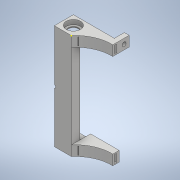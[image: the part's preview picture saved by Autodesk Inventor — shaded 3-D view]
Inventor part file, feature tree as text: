
AUTODESK INVENTOR PART (.ipt)
format: ipt  version: 2020 (Build 240168000, 168)  size: 626,176 bytes
history: native  units: mm
features: extrude x22, sketch x22, fillet x4
ambient origin geometry x8: Origin, YZ Plane, XZ Plane, XY Plane, X Axis, Y Axis, Z Axis, Center Point
bodies: Solid1 (feature_tree)
feature tree (48):
  extrude  "Extrusion1"  Depth=165.0mm
  extrude  "Extrusion2"  Depth=8.5mm
  extrude  "Extrusion3"  Depth=25.0mm TaperAngle=0.0deg
  extrude  "Extrusion4"  Depth=22.75mm
  extrude  "Extrusion5"  Depth=7.1mm
  extrude  "Extrusion6"  Depth=7.1mm TaperAngle=0.0deg
  fillet  "Fillet1"  Radius=5.0mm
  extrude  "Extrusion7"  Depth=10.0mm TaperAngle=0.0deg
  fillet  "Fillet2"  Radius=2.0mm
  extrude  "Extrusion8"  Depth=8.0mm
  extrude  "Extrusion9"  Depth=16.0mm
  fillet  "Fillet3"  Radius=8.0mm
  extrude  "Extrusion10"  Depth=6.0mm
  extrude  "Extrusion11"  Depth=12.25mm
  fillet  "Fillet4"  Radius=12.25mm
  extrude  "Extrusion12"  Depth=12.25mm
  extrude  "Extrusion13"  Depth=12.25mm
  extrude  "Extrusion14"  Depth=40.0mm
  sketch  "Sketch16"  dims[d40=2.0mm d41=8.0mm]
  extrude  "Extrusion15"  Depth=8.0mm
  extrude  "Extrusion16"  Depth=2.0mm
  extrude  "Extrusion17"  Depth=6.0mm
  extrude  "Extrusion18"  Depth=6.0mm
  extrude  "Extrusion19"  Depth=6.5mm TaperAngle=0.0deg
  extrude  "Extrusion20"  Depth=8.0mm TaperAngle=0.0deg
  extrude  "Extrusion21"  Depth=6.5mm
  extrude  "Extrusion22"  Depth=7.0mm TaperAngle=0.0deg
  sketch  "Sketch1"  dims[d0=25.0mm d1=165.0mm]
  sketch  "Sketch2"  dims[d2=3.0mm d3=0.0mm d4=8.5mm]
  sketch  "Sketch3"  dims[d5=8.5mm d6=25.0mm d7=0.0mm]
  sketch  "Sketch4"  dims[d8=25.0mm d9=22.75mm]
  sketch  "Sketch5"  dims[d10=7.1mm d11=0.0mm d12=15.5mm]
  sketch  "Sketch6"  dims[d13=165.0mm d14=0.0mm d15=7.1mm d16=0.0mm d17=5.0mm]
  sketch  "Sketch7"  dims[d18=5.0mm d19=10.0mm d20=0.0mm d21=2.0mm]
  sketch  "Sketch8"  dims[d22=16.0mm d23=8.0mm]
  sketch  "Sketch9"  dims[d24=16.0mm d25=16.0mm d26=8.0mm]
  sketch  "Sketch10"  dims[d27=45.0mm d28=0.0mm d29=6.0mm]
  sketch  "Sketch11"  dims[d30=12.25mm d31=3.5mm d32=12.25mm]
  sketch  "Sketch13"  dims[d33=3.5mm d34=12.25mm]
  sketch  "Sketch14"  dims[d35=12.25mm d36=3.5mm]
  sketch  "Sketch15"  dims[d37=40.0mm d38=0.0mm d39=1.0mm]
  sketch  "Sketch17"  dims[d42=1.0mm d43=2.0mm]
  sketch  "Sketch18"  dims[d44=12.0mm d45=0.0mm d46=6.0mm]
  sketch  "Sketch19"  dims[d47=6.0mm d48=4.0mm]
  sketch  "Sketch20"  dims[d49=8.0mm d50=6.5mm d51=0.0mm]
  sketch  "Sketch21"  dims[d52=6.35mm d53=8.0mm d54=0.0mm]
  sketch  "Sketch22"  dims[d55=6.5mm d56=47.0mm]
  sketch  "Sketch23"  dims[d57=1.0mm d58=7.0mm d59=0.0mm d60=7.1mm d61=0.0mm d62=14.5mm d63=0.0mm d64=2.0mm d65=0.0mm d66=8.5mm d67=2.0mm d68=0.0mm d69=20.0mm d70=0.0mm d71=165.0mm d72=0.0mm d73=22.6mm d74=8.5mm d75=0.0mm d76=22.6mm d77=8.5mm d78=0.0mm d79=20.0mm d80=7.5mm d81=0.0mm d82=6.25mm d83=7.5mm d84=0.0mm]
